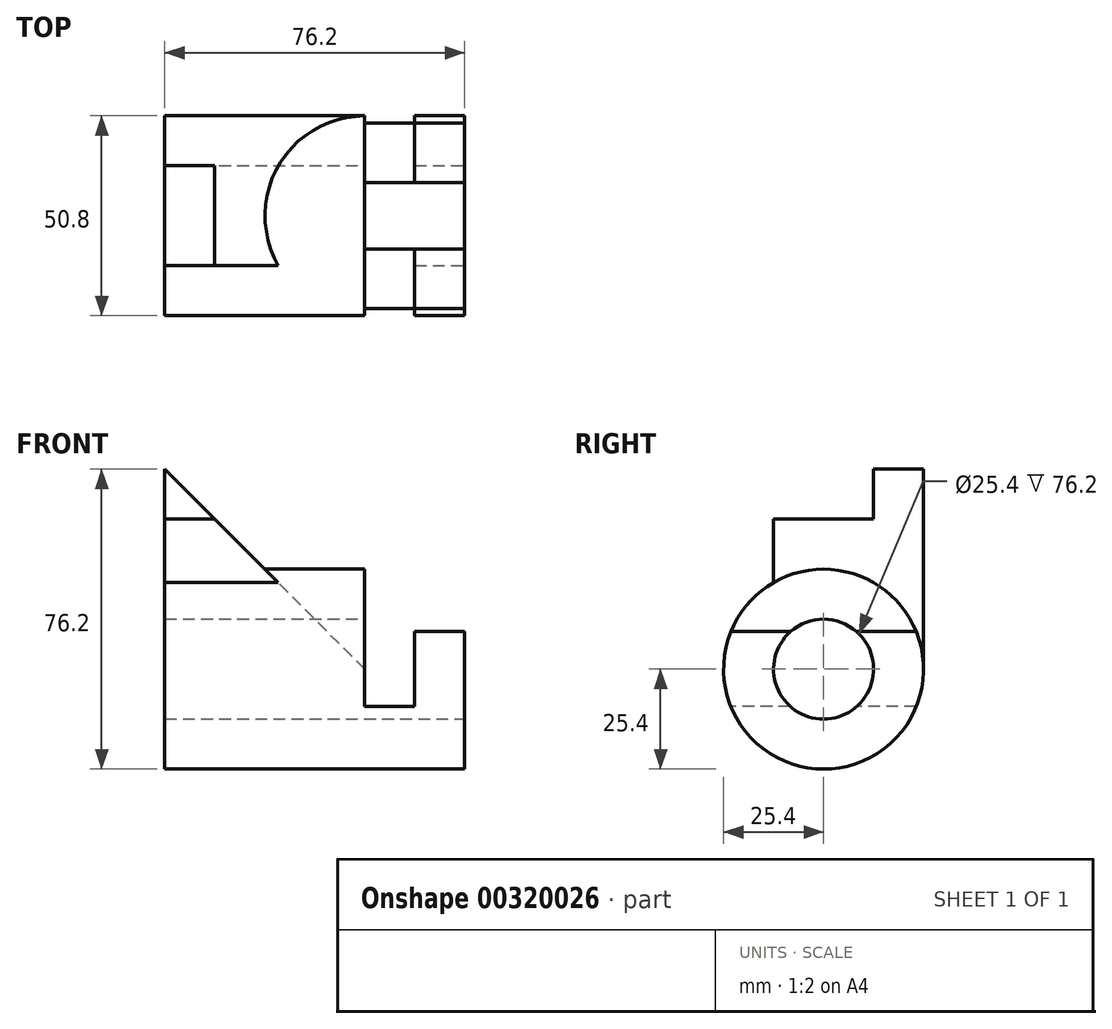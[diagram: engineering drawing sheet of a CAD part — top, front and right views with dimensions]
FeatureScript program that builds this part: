
annotation { "Feature Type Name" : "Feature", "Feature Type Description" : "" }
export const myFeature = defineFeature(function(context is Context, id is Id, definition is map)
    precondition{}
    {
        {
            var Q0;
            Q0=qCreatedBy(makeId("Right.planeOp"),FACE);
            var sketch = newSketch(context, id + "F0", { "sketchPlane" : qUnion([Q0])});
            skCircle(sketch, "E0", {"center": v(0, 0) * mm, "radius": 12.7 * mm});
            skCircle(sketch, "E1", {"center": v(0, 0) * mm, "radius": 25.4 * mm});
            skLineSegment(sketch, "E2", {"start": v(-12.7, 22) * mm, "end": v(-12.7, 38.38) * mm});
            skLineSegment(sketch, "E3", {"start": v(-12.7, 38.38) * mm, "end": v(12.7, 38.38) * mm});
            skLineSegment(sketch, "E4", {"start": v(12.7, 38.38) * mm, "end": v(12.7, 50.8) * mm});
            skLineSegment(sketch, "E5", {"start": v(12.7, 50.8) * mm, "end": v(25.4, 50.8) * mm});
            skLineSegment(sketch, "E6", {"start": v(25.4, 50.8) * mm, "end": v(25.4, 0) * mm});
            skSolve(sketch);
        }
        {
            var Q0;
            Q0=makeQuery(id+"F0.imprint","IMPRINT",FACE,{"disambiguationData":[TD([[makeQuery(id+"F0.imprint","IMPRINT",EDGE,{"derivedFrom":sQuery(id+"F0.wireOp",EDGE,"E0")}),-1.0]])]});
            extrude(context, id + "F1", {"entities" : qUnion([Q0]), "oppositeDirection" : true, "depth" : 76.2 * mm});
        }
        {
            var Q0;
            Q0=qCreatedBy(makeId("Front.planeOp"),FACE);
            var sketch = newSketch(context, id + "F2", { "sketchPlane" : qUnion([Q0])});
            skLineSegment(sketch, "E7", {"start": v(-76.2, -25.4) * mm, "end": v(0, -25.4) * mm});
            skLineSegment(sketch, "E8", {"start": v(0, -25.4) * mm, "end": v(0, 9.53) * mm});
            skLineSegment(sketch, "E9", {"start": v(0, 9.53) * mm, "end": v(-12.7, 9.53) * mm});
            skLineSegment(sketch, "E10", {"start": v(-12.7, 9.53) * mm, "end": v(-12.7, -9.53) * mm});
            skLineSegment(sketch, "E11", {"start": v(-12.7, -9.53) * mm, "end": v(-25.4, -9.53) * mm});
            skLineSegment(sketch, "E12", {"start": v(-76.2, 50.8) * mm, "end": v(-76.2, -25.4) * mm});
            skLineSegment(sketch, "E13.top", {"start": v(-76.2, 50.8) * mm, "end": v(0, 50.8) * mm});
            skLineSegment(sketch, "E13.left", {"start": v(-76.2, -25.4) * mm, "end": v(-76.2, 50.8) * mm});
            skLineSegment(sketch, "E13.right", {"start": v(0, -25.4) * mm, "end": v(0, 50.8) * mm});
            skLineSegment(sketch, "E14", {"start": v(-76.2, 50.8) * mm, "end": v(-25.4, 0) * mm});
            skLineSegment(sketch, "E15", {"start": v(-76.2, 20.32) * mm, "end": v(-45.72, 20.32) * mm});
            skLineSegment(sketch, "E16", {"start": v(-50.8, 25.4) * mm, "end": v(-25.4, 25.4) * mm});
            skLineSegment(sketch, "E17", {"start": v(0, 25.4) * mm, "end": v(-76.2, 25.4) * mm, "construction": true});
            skLineSegment(sketch, "E18", {"start": v(-25.4, -9.53) * mm, "end": v(-25.4, 25.4) * mm});
            skLineSegment(sketch, "E19", {"start": v(0, 25.4) * mm, "end": v(0, 9.53) * mm});
            skLineSegment(sketch, "E20", {"start": v(-76.2, 38.1) * mm, "end": v(-63.5, 38.1) * mm});
            skLineSegment(sketch, "E21", {"start": v(-25.4, 0) * mm, "end": v(-76.2, 0) * mm});
            skLineSegment(sketch, "E22", {"start": v(-76.2, 0) * mm, "end": v(-76.2, 50.8) * mm});
            skSolve(sketch);
        }
        {
            var Q0;
            Q0=makeQuery(id+"F2.imprint","IMPRINT",FACE,{"disambiguationData":[TD([[makeQuery(id+"F2.imprint","IMPRINT",EDGE,{"derivedFrom":sQuery(id+"F2.wireOp",EDGE,"E9")}),-1.0]])]});
            extrude(context, id + "F3", {"entities" : qUnion([Q0]), "operationType" : NewBodyOperationType.REMOVE, "endBound" : BoundingType.SYMMETRIC, "oppositeDirection" : true, "depth" : 101.6 * mm});
        }
        {
            var Q0;
            {var subQ0=sQuery(id+"F2.wireOp",EDGE,"E15");Q0=makeQuery(id+"F2.imprint","IMPRINT",FACE,{"disambiguationData":[TD([[makeQuery(id+"F2.imprint","IMPRINT",EDGE,{"derivedFrom":subQ0}),1.0]])]});}
            extrude(context, id + "F4", {"entities" : qUnion([Q0]), "operationType" : NewBodyOperationType.ADD, "endBound" : BoundingType.SYMMETRIC, "depth" : 25.4 * mm});
        }
        {
            var Q0;
            {var subQ3=sQuery(id+"F2.wireOp",EDGE,"E20");Q0=makeQuery(id+"F2.imprint","IMPRINT",FACE,{"disambiguationData":[TD([[makeQuery(id+"F2.imprint","IMPRINT",EDGE,{"derivedFrom":subQ3}),1.0]])]});}
            var Q1;
            {var subQ0=sQuery(id+"F2.wireOp",EDGE,"E15");Q1=makeQuery(id+"F2.imprint","IMPRINT",FACE,{"disambiguationData":[TD([[makeQuery(id+"F2.imprint","IMPRINT",EDGE,{"derivedFrom":subQ0}),1.0]])]});}
            extrude(context, id + "F5", {"entities" : qUnion([Q0, Q1]), "operationType" : NewBodyOperationType.ADD, "oppositeDirection" : true, "depth" : 25.4 * mm});
        }
        {
            var Q0;
            Q0=makeQuery(id+"F5.opExtrude","CAP_FACE",FACE,{"disambiguationData":[OSD([sQuery(id+"F2.wireOp",EDGE,"E13.left"),sQuery(id+"F2.wireOp",EDGE,"E14"),sQuery(id+"F2.wireOp",EDGE,"E15")])],"isStart":true});
            extrude(context, id + "F6", {"entities" : qUnion([Q0]), "operationType" : NewBodyOperationType.REMOVE, "oppositeDirection" : true, "depth" : 12.7 * mm});
        }
        {
            var Q0;
            {var subQ2=sQuery(id+"F2.wireOp",EDGE,"E15");Q0=makeQuery(id+"F2.imprint","IMPRINT",FACE,{"disambiguationData":[TD([[makeQuery(id+"F2.imprint","IMPRINT",EDGE,{"derivedFrom":subQ2}),-1.0]])]});}
            var Q1;
            Q1=makeQuery(id+"F5.opExtrude","CAP_FACE",FACE,{"disambiguationData":[OSD([sQuery(id+"F2.wireOp",EDGE,"E14"),sQuery(id+"F2.wireOp",EDGE,"E15"),sQuery(id+"F2.wireOp",EDGE,"E22")])],"isStart":false});
            extrude(context, id + "F7", {"entities" : qUnion([Q0]), "operationType" : NewBodyOperationType.ADD, "endBound" : BoundingType.UP_TO_SURFACE, "oppositeDirection" : true, "endBoundEntityFace" : qUnion([Q1]), "depth" : 25.4 * mm});
        }
        {
            var Q0;
            Q0=makeQuery(id+"F0.imprint","IMPRINT",FACE,{"disambiguationData":[TD([[makeQuery(id+"F0.imprint","IMPRINT",EDGE,{"derivedFrom":sQuery(id+"F0.wireOp",EDGE,"E0")}),1.0]])]});
            var Q1;
            {var subQ0=sQuery(id+"F2.wireOp",EDGE,"E22");Q1=makeQuery(id+"F7.boolean.opBoolean","MERGE",FACE,{"derivedFrom":[makeQuery(id+"F5.boolean.opBoolean","MERGE",FACE,{"derivedFrom":[makeQuery(id+"F4.boolean.opBoolean","MERGE",FACE,{"derivedFrom":[makeQuery(id+"F1.opExtrude","CAP_FACE",FACE,{"disambiguationData":[OSD([sQuery(id+"F0.wireOp",EDGE,"E0"),sQuery(id+"F0.wireOp",EDGE,"E1")])],"isStart":false}),makeQuery(id+"F4.opExtrude","SWEPT_FACE",FACE,{"disambiguationData":[OSD([subQ0])]})]}),makeQuery(id+"F5.opExtrude","SWEPT_FACE",FACE,{"disambiguationData":[OSD([subQ0])]})]}),makeQuery(id+"F7.opExtrude","SWEPT_FACE",FACE,{"disambiguationData":[OSD([subQ0])]})]});}
            extrude(context, id + "F8", {"entities" : qUnion([Q0]), "operationType" : NewBodyOperationType.REMOVE, "endBound" : BoundingType.UP_TO_SURFACE, "oppositeDirection" : true, "endBoundEntityFace" : qUnion([Q1]), "depth" : 25.4 * mm});
        }
    });
